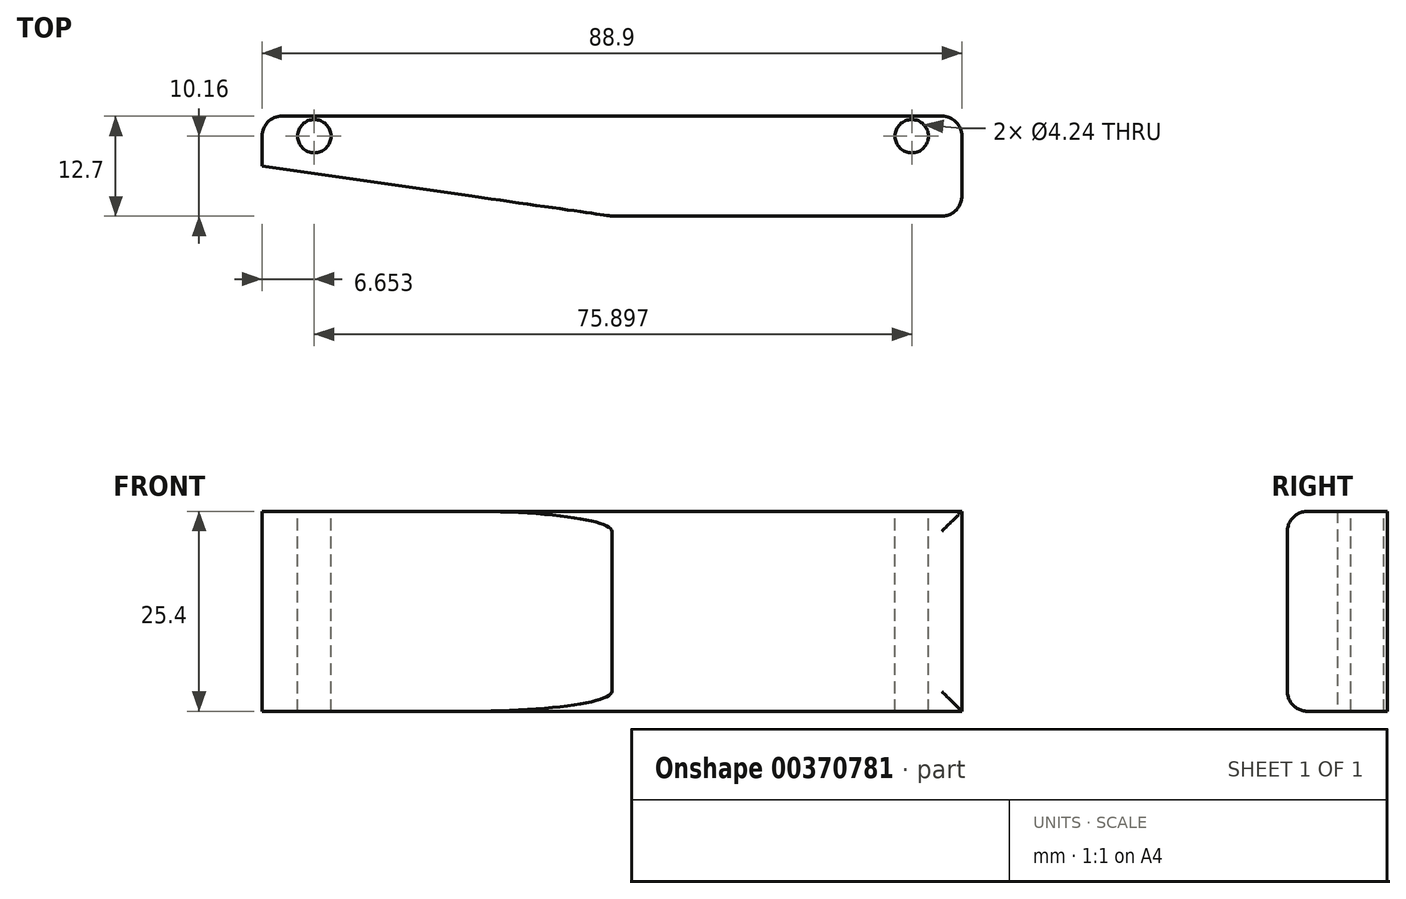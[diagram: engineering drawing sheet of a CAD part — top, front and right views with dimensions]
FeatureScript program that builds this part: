
annotation { "Feature Type Name" : "Feature", "Feature Type Description" : "" }
export const myFeature = defineFeature(function(context is Context, id is Id, definition is map)
    precondition{}
    {
        {
            var Q0;
            Q0=qCreatedBy(makeId("Front.planeOp"),FACE);
            var sketch = newSketch(context, id + "F0", { "sketchPlane" : qUnion([Q0])});
            skLineSegment(sketch, "E0.bottom", {"start": v(0, 0) * mm, "end": v(88.9, 0) * mm});
            skLineSegment(sketch, "E0.top", {"start": v(0, 25.4) * mm, "end": v(88.9, 25.4) * mm});
            skLineSegment(sketch, "E0.left", {"start": v(0, 0) * mm, "end": v(0, 25.4) * mm});
            skLineSegment(sketch, "E0.right", {"start": v(88.9, 0) * mm, "end": v(88.9, 25.4) * mm});
            skSolve(sketch);
        }
        {
            var Q0;
            Q0=makeQuery(id+"F0.imprint","IMPRINT",FACE,{"disambiguationData":[TD([[makeQuery(id+"F0.imprint","IMPRINT",EDGE,{"derivedFrom":sQuery(id+"F0.wireOp",EDGE,"E0.bottom")}),1.0]])]});
            extrude(context, id + "F1", {"entities" : qUnion([Q0]), "depth" : 12.7 * mm});
        }
        {
            var Q0;
            Q0=makeQuery(id+"F1.opExtrude","SWEPT_FACE",FACE,{"disambiguationData":[OSD([sQuery(id+"F0.wireOp",EDGE,"E0.bottom")])]});
            var sketch = newSketch(context, id + "F2", { "sketchPlane" : qUnion([Q0])});
            skLineSegment(sketch, "E1", {"start": v(44.45, 12.7) * mm, "end": v(0, 6.35) * mm});
            skSolve(sketch);
        }
        {
            var Q0;
            {var subQ0=sQuery(id+"F2.wireOp",EDGE,"E1");Q0=makeQuery(id+"F2.imprint","IMPRINT",FACE,{"disambiguationData":[TD([[makeQuery(id+"F2.imprint","IMPRINT",EDGE,{"derivedFrom":subQ0}),-1.0]])]});}
            extrude(context, id + "F3", {"entities" : qUnion([Q0]), "operationType" : NewBodyOperationType.REMOVE, "oppositeDirection" : true, "depth" : 25.4 * mm});
        }
        {
            var Q0;
            Q0=makeQuery(id+"F1.opExtrude","CAP_EDGE",EDGE,{"disambiguationData":[OSD([sQuery(id+"F0.wireOp",EDGE,"E0.left")])],"isStart":true});
            var Q1;
            Q1=makeQuery(id+"F3.boolean.opBoolean","COPY",EDGE,{"derivedFrom":makeQuery(id+"F3.opExtrude","SWEPT_EDGE",EDGE,{"disambiguationData":[OSD([sQuery(id+"F0.wireOp",EDGE,"E0.bottom"),sQuery(id+"F0.wireOp",EDGE,"E0.left"),sQuery(id+"F2.wireOp",EDGE,"E1")])]})});
            var Q2;
            Q2=makeQuery(id+"F1.opExtrude","CAP_EDGE",EDGE,{"disambiguationData":[OSD([sQuery(id+"F0.wireOp",EDGE,"E0.right")])],"isStart":true});
            var Q3;
            Q3=makeQuery(id+"F1.opExtrude","CAP_EDGE",EDGE,{"disambiguationData":[OSD([sQuery(id+"F0.wireOp",EDGE,"E0.bottom")])],"isStart":false});
            var Q4;
            Q4=makeQuery(id+"F1.opExtrude","CAP_EDGE",EDGE,{"disambiguationData":[OSD([sQuery(id+"F0.wireOp",EDGE,"E0.top")])],"isStart":false});
            var Q5;
            Q5=makeQuery(id+"F1.opExtrude","CAP_EDGE",EDGE,{"disambiguationData":[OSD([sQuery(id+"F0.wireOp",EDGE,"E0.right")])],"isStart":false});
            var Q6;
            Q6=makeQuery(id+"F3.boolean.opBoolean","COPY",EDGE,{"derivedFrom":makeQuery(id+"F3.opExtrude","SWEPT_EDGE",EDGE,{"disambiguationData":[OSD([sQuery(id+"F0.wireOp",EDGE,"E0.bottom"),sQuery(id+"F2.wireOp",EDGE,"E1")])]})});
            fillet(context, id + "F4", {"entities" : qUnion([Q0, Q1, Q2, Q3, Q4, Q5, Q6]), "radius" : 2.54 * mm, "tangentPropagation" : true, "allowEdgeOverflow" : false});
        }
        {
            var Q0;
            Q0=makeQuery(id+"F1.opExtrude","SWEPT_FACE",FACE,{"disambiguationData":[OSD([sQuery(id+"F0.wireOp",EDGE,"E0.top")])]});
            var sketch = newSketch(context, id + "F5", { "sketchPlane" : qUnion([Q0])});
            skCircle(sketch, "E2", {"center": v(82.55, -2.54) * mm, "radius": 2.12 * mm});
            skCircle(sketch, "E3", {"center": v(6.65, -2.54) * mm, "radius": 2.12 * mm});
            skSolve(sketch);
        }
        {
            var Q0;
            Q0=makeQuery(id+"F5.imprint","IMPRINT",FACE,{"disambiguationData":[TD([[makeQuery(id+"F5.imprint","IMPRINT",EDGE,{"derivedFrom":sQuery(id+"F5.wireOp",EDGE,"E2")}),1.0]])]});
            var Q1;
            Q1=makeQuery(id+"F5.imprint","IMPRINT",FACE,{"disambiguationData":[TD([[makeQuery(id+"F5.imprint","IMPRINT",EDGE,{"derivedFrom":sQuery(id+"F5.wireOp",EDGE,"E3")}),1.0]])]});
            extrude(context, id + "F6", {"entities" : qUnion([Q0, Q1]), "operationType" : NewBodyOperationType.REMOVE, "oppositeDirection" : true, "depth" : 26.16 * mm});
        }
    });
